# Revit family: Genelec_3440
name_source: partatom
category: Generic Models
units: mm (PartAtom-declared; Revit-internal decimal feet)

## family parameters
Always vertical = No
Can host rebar = No
Cut with Voids When Loaded = No
Maintain Annotation Orientation = No
Part Type = Normal
Room Calculation Point = Yes
Round Connector Dimension = Use Diameter
Shared = No
Work Plane-Based = No

## types (1)
- 3440A
    Accuracy of Frequency Response = ± 3 dB (35 Hz - 120 Hz)
    Acoustic Axis = 0
    BIMobject category = Audio Electronics
    Color = Genelec Black
    Connections = 1 x RJ45 AES67 / Dante Input (Smart IP Manager and PoE Power)
1 x Euroblock Analog Input
    Default Elevation = 0 mm  [stored 0 ft]
    Depth = 220 mm  [stored 0.721785 ft]
    Description = The 3440A Smart IP Active PoE Powered Subwoofer enhances the versatile Smart IP family of loudspeakers. By redefining the reference for low-frequency output using PoE power, the subwoofer pushes installation audio quality to new greater heights of performance.
    Driver Dimensions = ⌀ 165 mm Woofer
    Export Type to IFC As = IfcAudioVisualApplianceType
    Finish Type = Painted MDF
    Frequency Response = 35 Hz - 120 Hz (- 6 dB)
    Height = 475 mm  [stored 1.5584 ft]
    IFC Classification = Electric Appliance
    IFC Name = 3440A
    Line Drawing = https://assets.ctfassets.net
    Mains Voltage = PoE+/PoE
    Manufacturer = GENELEC
    Manufacturer Country = Finland
    Max. short term sine wave acoustic output  on axis in half space, averaged from 100Hz to 3 kHz = ≥ 106 dB SPL
    Maximum long term RMS acoustic output in same conditions with IEC weighted noise (limited by driver unit protection circuit) = ≥ 101 dB SPL
    Model = 3440
    Model Description = Smart IP Active Subwoofer
    Model Image = https://images.ctfassets.net
    Model Name = 3440A
    Mounting Type = Separate Wall and Ceiling Mount 3440-400B
    Power Consumption = 30 W
    Power consumption Idle = ≤5 W
    Power consumption Standby = ≤4W (ISS Active)
    Price List Description = Smart IP active subwoofer in MDF cabinet with the driver protected inside the cabinet. Freestanding installation or easy optional installation bracket for wall and ceiling installations. Woofer driver 165 mm (6.5 in). Class D amplifier 70 W with integrated Smart IP crossover inside the loudspeaker. Maximum output 106 dB SPL, frequency response 35 Hz - 120 kHz (-6 dB). Compatible with PoE+ (30W) and PoE (15W). API for automation systems. Setup using Smart IP Manager software, offering device discovery, room equalisation, zone organisation and status monitoring. Dimensions : Length 475 mm, Width 475 mm, Depth 220 mm / Length 18.75 in x Width 18.75 in x Depth 8.75 in. Weight: 14.5 kg (32 lb)
    Product Family = Installation Louspeaker
    Product Group = 3000 Series Installation Loudspeakers
    Self-generated Noise = ≤5 dB
    Type IFC Predefined Type = SPEAKER
    Type Image = <None>
    URL = https://www.genelec.com
    Uniclass 2.0 Description = Sound Amplifiers
    Weight = 14.5
    Width = 475 mm  [stored 1.5584 ft]

note: [stored X ft] marks values corroborated as IEEE doubles in the binary element streams (Revit-internal decimal feet)

## geometry (parser evidence)
native form markers: Sweep x2
no freeform markers — native parametric forms only
